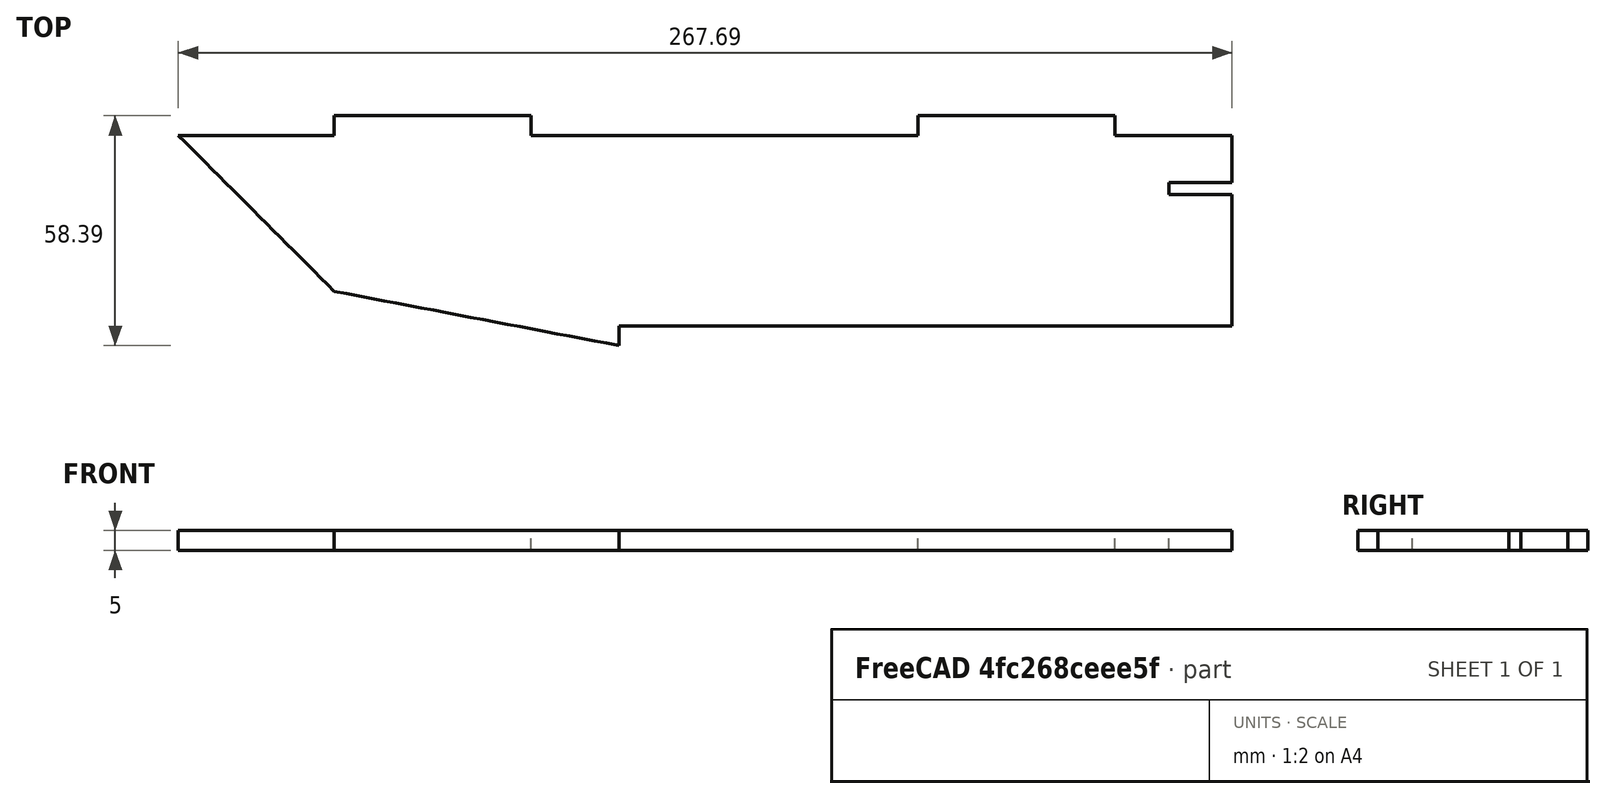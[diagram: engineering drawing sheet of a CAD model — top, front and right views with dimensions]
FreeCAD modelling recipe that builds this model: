
FCSTD DOCUMENT  (FreeCAD 0.19R)
Label: F-35_v2_parts_10
License: All rights reserved
LicenseURL: http://en.wikipedia.org/wiki/All_rights_reserved
objects: PartDesign::CoordinateSystem×3, App::DocumentObjectGroup×2, App::FeaturePython×1, Sketcher::SketchObject×1, PartDesign::Pad×1, PartDesign::Body×1, App::Part×1
note: 7 computed .brp shape members not serialized (recipe doc carries the construction recipe); baked Part::Feature solids carry a one-line shape summary decoded from their .brp

FEATURE [App::DocumentObjectGroup] Parts
FEATURE [PartDesign::CoordinateSystem] LCS_Origin
  AttacherType = Attacher::AttachEngine3D
  MapMode = 2
  Support = -> [X_Axis]
FEATURE [App::DocumentObjectGroup] Constraints
FEATURE [App::FeaturePython] Variables  # WARN: FeaturePython — macro-defined, semantics opaque (R4)
FEATURE [Sketcher::SketchObject] Sketch009
  FullyConstrained = false
  sketch-geometry (18):
    g0: BSplineCurve PolesCount=2 KnotsCount=2 Degree=1 IsPeriodic=0
    g1: BSplineCurve PolesCount=2 KnotsCount=2 Degree=1 IsPeriodic=0
    g2: BSplineCurve PolesCount=2 KnotsCount=2 Degree=1 IsPeriodic=0
    g3: BSplineCurve PolesCount=2 KnotsCount=2 Degree=1 IsPeriodic=0
    g4: BSplineCurve PolesCount=2 KnotsCount=2 Degree=1 IsPeriodic=0
    g5: BSplineCurve PolesCount=2 KnotsCount=2 Degree=1 IsPeriodic=0
    g6: BSplineCurve PolesCount=2 KnotsCount=2 Degree=1 IsPeriodic=0
    g7: BSplineCurve PolesCount=2 KnotsCount=2 Degree=1 IsPeriodic=0
    g8: BSplineCurve PolesCount=2 KnotsCount=2 Degree=1 IsPeriodic=0
    g9: BSplineCurve PolesCount=2 KnotsCount=2 Degree=1 IsPeriodic=0
    g10: BSplineCurve PolesCount=2 KnotsCount=2 Degree=1 IsPeriodic=0
    g11: BSplineCurve PolesCount=2 KnotsCount=2 Degree=1 IsPeriodic=0
    g12: BSplineCurve PolesCount=2 KnotsCount=2 Degree=1 IsPeriodic=0
    g13: BSplineCurve PolesCount=2 KnotsCount=2 Degree=1 IsPeriodic=0
    g14: BSplineCurve PolesCount=2 KnotsCount=2 Degree=1 IsPeriodic=0
    g15: BSplineCurve PolesCount=2 KnotsCount=2 Degree=1 IsPeriodic=0
    g16: BSplineCurve PolesCount=2 KnotsCount=2 Degree=1 IsPeriodic=0
    g17: BSplineCurve PolesCount=2 KnotsCount=2 Degree=1 IsPeriodic=0
FEATURE [PartDesign::Pad] Pad008
  Direction = (1,1,1)
  Length = 5
  Length2 = 100
  Profile = -> Sketch009
  Type = 0
FEATURE [PartDesign::Body] Body009  label="Part10"
  Group = -> [Sketch009,Pad008]
  Origin = -> Origin010
  Tip = -> Pad008
FEATURE [PartDesign::CoordinateSystem] LCS_1
  AttacherType = Attacher::AttachEngine3D
  MapMode = 7
  Placement = pos=(147.086,-550.773,0) rot=(0,1,0;3.14159rad)
  Support = -> [Pad008]
FEATURE [PartDesign::CoordinateSystem] LCS_2
  AttacherType = Attacher::AttachEngine3D
  MapMode = 7
  Placement = pos=(375.156,-599.139,5) rot=(0.57735,0.57735,0.57735;2.0944rad)
  Support = -> [Pad008]
FEATURE [App::Part] Model
  Configuration = 0
  Group = -> [LCS_Origin,Constraints,Variables,Body009,LCS_1,LCS_2]
  Origin = -> Origin
  Type = Assembly4 Model
